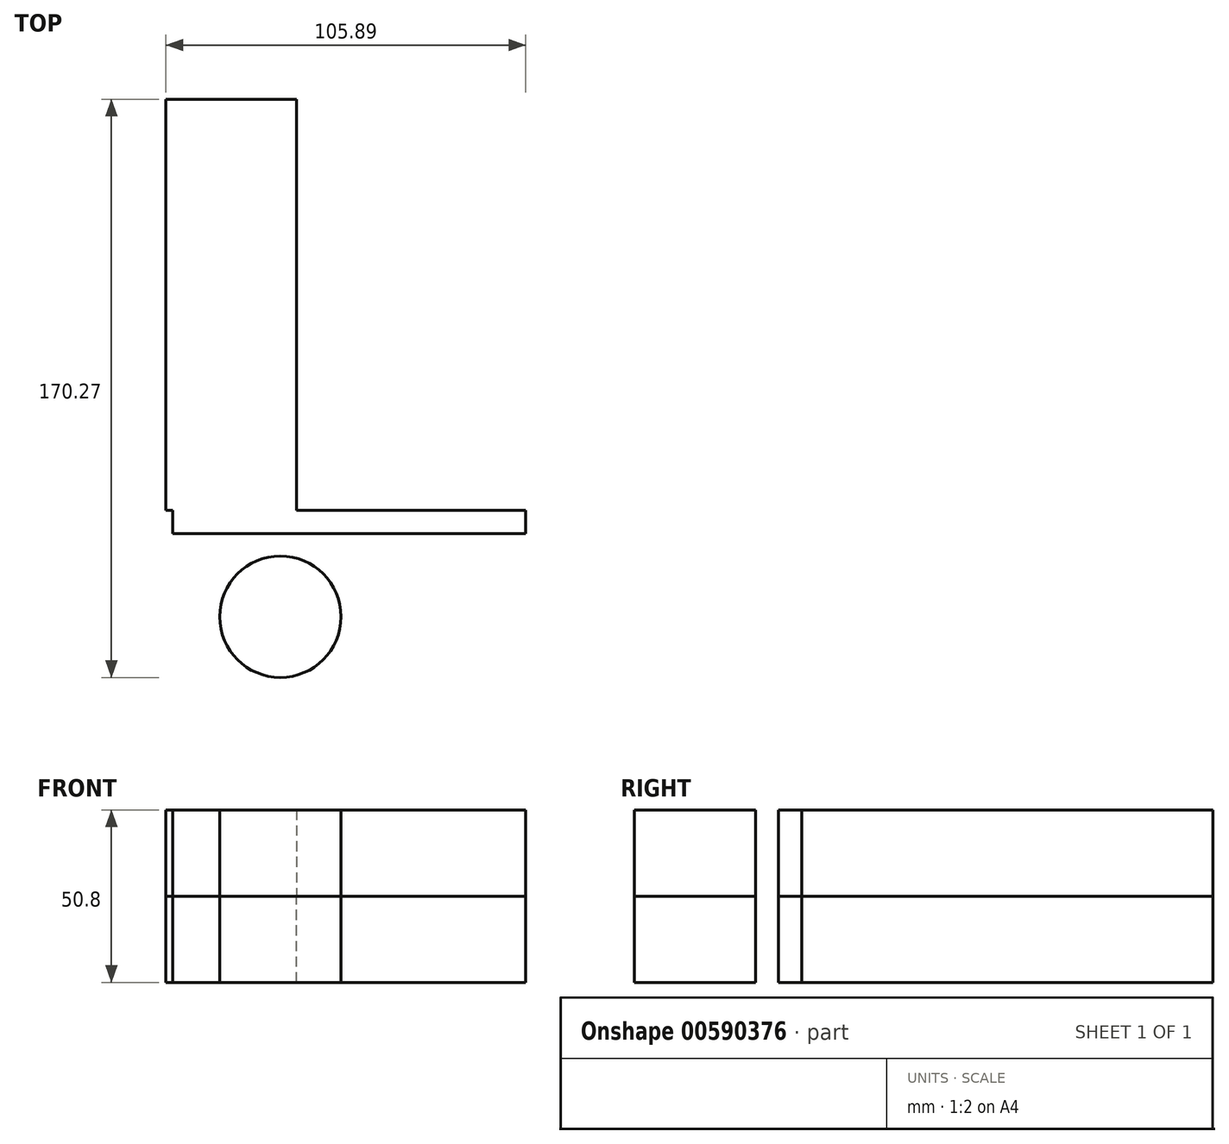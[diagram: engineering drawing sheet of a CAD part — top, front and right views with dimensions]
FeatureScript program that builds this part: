
annotation { "Feature Type Name" : "Feature", "Feature Type Description" : "" }
export const myFeature = defineFeature(function(context is Context, id is Id, definition is map)
    precondition{}
    {
        {
            var Q0;
            Q0=qCreatedBy(makeId("Top.planeOp"),FACE);
            var sketch = newSketch(context, id + "F0", { "sketchPlane" : qUnion([Q0])});
            skLineSegment(sketch, "E0.bottom", {"start": v(42.76, -40.45) * mm, "end": v(-61.1, -40.45) * mm});
            skLineSegment(sketch, "E0.top", {"start": v(42.76, -33.6) * mm, "end": v(-61.1, -33.6) * mm});
            skLineSegment(sketch, "E0.left", {"start": v(42.76, -40.45) * mm, "end": v(42.76, -33.6) * mm});
            skLineSegment(sketch, "E0.right", {"start": v(-61.1, -40.45) * mm, "end": v(-61.1, -33.6) * mm});
            skLineSegment(sketch, "E1.bottom", {"start": v(-24.67, -33.6) * mm, "end": v(-63.13, -33.6) * mm});
            skLineSegment(sketch, "E1.top", {"start": v(-24.67, 87.42) * mm, "end": v(-63.13, 87.42) * mm});
            skLineSegment(sketch, "E1.left", {"start": v(-24.67, -33.6) * mm, "end": v(-24.67, 87.42) * mm});
            skLineSegment(sketch, "E1.right", {"start": v(-63.13, -33.6) * mm, "end": v(-63.13, 87.42) * mm});
            skCircle(sketch, "E2", {"center": v(-29.44, -64.99) * mm, "radius": 17.87 * mm});
            skSolve(sketch);
        }
        {
            var Q0;
            Q0 = qSketchRegion(id + "F0", true);
            extrude(context, id + "F1", {"entities" : qUnion([Q0]), "oppositeDirection" : true, "depth" : 25.4 * mm, "offsetDistance" : 25.4 * mm});
        }
        {
            var Q0;
            Q0 = qSketchRegion(id + "F0", true);
            extrude(context, id + "F2", {"entities" : qUnion([Q0]), "depth" : 25.4 * mm, "offsetDistance" : 25.4 * mm});
        }
    });
